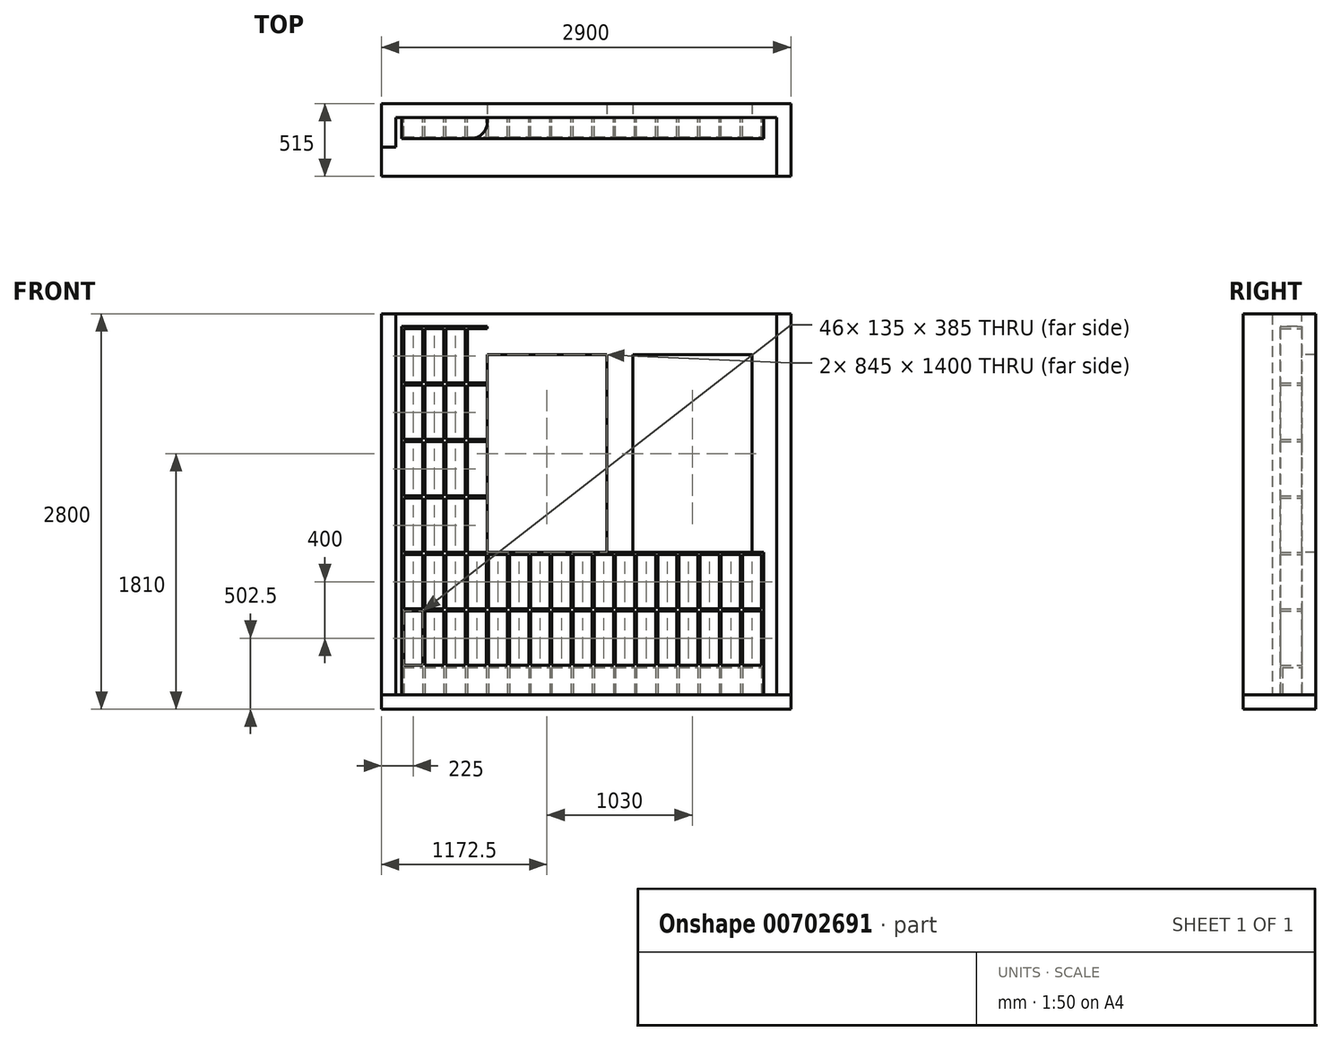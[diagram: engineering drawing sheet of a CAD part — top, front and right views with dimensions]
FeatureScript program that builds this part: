
annotation { "Feature Type Name" : "Feature", "Feature Type Description" : "" }
export const myFeature = defineFeature(function(context is Context, id is Id, definition is map)
    precondition{}
    {
        {
            var Q0;
            Q0=qCreatedBy(makeId("Front.planeOp"),FACE);
            var sketch = newSketch(context, id + "F0", { "sketchPlane" : qUnion([Q0])});
            skLineSegment(sketch, "E0.bottom", {"start": v(1350, -1350) * mm, "end": v(-1350, -1350) * mm});
            skLineSegment(sketch, "E0.top", {"start": v(1350, 1350) * mm, "end": v(-1350, 1350) * mm});
            skLineSegment(sketch, "E0.left", {"start": v(1350, -1350) * mm, "end": v(1350, 1350) * mm});
            skLineSegment(sketch, "E0.right", {"start": v(-1350, -1350) * mm, "end": v(-1350, 1350) * mm});
            skPoint(sketch, "E0.middle", {"position": v(0, 0) * mm});
            skLineSegment(sketch, "E1.bottom", {"start": v(1175, -340) * mm, "end": v(330, -340) * mm});
            skLineSegment(sketch, "E1.top", {"start": v(1175, 1060) * mm, "end": v(330, 1060) * mm});
            skLineSegment(sketch, "E1.left", {"start": v(1175, -340) * mm, "end": v(1175, 1060) * mm});
            skLineSegment(sketch, "E1.right", {"start": v(330, -340) * mm, "end": v(330, 1060) * mm});
            skPoint(sketch, "E1.middle", {"position": v(752.5, 360) * mm});
            skLineSegment(sketch, "E2.bottom", {"start": v(145, -340) * mm, "end": v(-700, -340) * mm});
            skLineSegment(sketch, "E2.top", {"start": v(145, 1060) * mm, "end": v(-700, 1060) * mm});
            skLineSegment(sketch, "E2.left", {"start": v(145, -340) * mm, "end": v(145, 1060) * mm});
            skLineSegment(sketch, "E2.right", {"start": v(-700, -340) * mm, "end": v(-700, 1060) * mm});
            skSolve(sketch);
        }
        {
            var Q0;
            Q0 = qSketchRegion(id + "F0", true);
            extrude(context, id + "F1", {"entities" : qUnion([Q0]), "oppositeDirection" : true, "depth" : 100 * mm, "offsetDistance" : 25 * mm});
        }
        {
            var Q0;
            Q0=qCreatedBy(makeId("Front.planeOp"),FACE);
            var sketch = newSketch(context, id + "F2", { "sketchPlane" : qUnion([Q0])});
            skLineSegment(sketch, "E3.top", {"start": v(-1307.5, -1350) * mm, "end": v(-1292.5, -1350) * mm});
            skLineSegment(sketch, "E4.top", {"start": v(-1157.5, -1350) * mm, "end": v(-1142.5, -1350) * mm});
            skLineSegment(sketch, "E5.MirrorCS", {"start": v(-992.5, -1350) * mm, "end": v(-1007.5, -1350) * mm});
            skLineSegment(sketch, "E6.MirrorCS", {"start": v(-842.5, -1350) * mm, "end": v(-857.5, -1350) * mm});
            skLineSegment(sketch, "E7.MirrorCS", {"start": v(-692.5, -355) * mm, "end": v(-692.5, -740) * mm});
            skLineSegment(sketch, "E8.MirrorCS", {"start": v(-557.5, -355) * mm, "end": v(-557.5, -740) * mm});
            skLineSegment(sketch, "E9.MirrorCS", {"start": v(-542.5, -355) * mm, "end": v(-542.5, -740) * mm});
            skLineSegment(sketch, "E10.MirrorCS", {"start": v(-707.5, -1350) * mm, "end": v(-692.5, -1350) * mm});
            skLineSegment(sketch, "E11.MirrorCS", {"start": v(-542.5, -1350) * mm, "end": v(-557.5, -1350) * mm});
            skLineSegment(sketch, "E12", {"start": v(-707.5, -340) * mm, "end": v(-692.5, -340) * mm});
            skLineSegment(sketch, "E13.trimOffspring", {"start": v(-707.5, -355) * mm, "end": v(-707.5, -740) * mm});
            skLineSegment(sketch, "E14", {"start": v(-557.5, -340) * mm, "end": v(-542.5, -340) * mm});
            skLineSegment(sketch, "E15.MirrorCS", {"start": v(-407.5, -355) * mm, "end": v(-407.5, -740) * mm});
            skLineSegment(sketch, "E16.MirrorCS", {"start": v(-392.5, -355) * mm, "end": v(-392.5, -740) * mm});
            skLineSegment(sketch, "E17.MirrorCS", {"start": v(-257.5, -355) * mm, "end": v(-257.5, -740) * mm});
            skLineSegment(sketch, "E18.MirrorCS", {"start": v(-242.5, -355) * mm, "end": v(-242.5, -740) * mm});
            skLineSegment(sketch, "E19.MirrorCS", {"start": v(-107.5, -355) * mm, "end": v(-107.5, -740) * mm});
            skLineSegment(sketch, "E20.MirrorCS", {"start": v(-92.5, -355) * mm, "end": v(-92.5, -740) * mm});
            skLineSegment(sketch, "E21", {"start": v(-257.5, -340) * mm, "end": v(-242.5, -340) * mm});
            skLineSegment(sketch, "E22", {"start": v(-407.5, -1350) * mm, "end": v(-392.5, -1350) * mm});
            skLineSegment(sketch, "E23", {"start": v(-257.5, -1350) * mm, "end": v(-242.5, -1350) * mm});
            skLineSegment(sketch, "E24", {"start": v(-107.5, -1350) * mm, "end": v(-92.5, -1350) * mm});
            skLineSegment(sketch, "E25.MirrorCS", {"start": v(42.5, -355) * mm, "end": v(42.5, -740) * mm});
            skLineSegment(sketch, "E26.MirrorCS", {"start": v(57.5, -355) * mm, "end": v(57.5, -740) * mm});
            skLineSegment(sketch, "E27.MirrorCS", {"start": v(192.5, -355) * mm, "end": v(192.5, -740) * mm});
            skLineSegment(sketch, "E28.MirrorCS", {"start": v(207.5, -355) * mm, "end": v(207.5, -740) * mm});
            skLineSegment(sketch, "E29.MirrorCS", {"start": v(342.5, -355) * mm, "end": v(342.5, -740) * mm});
            skLineSegment(sketch, "E30.MirrorCS", {"start": v(357.5, -355) * mm, "end": v(357.5, -740) * mm});
            skLineSegment(sketch, "E31.MirrorCS", {"start": v(492.5, -355) * mm, "end": v(492.5, -740) * mm});
            skLineSegment(sketch, "E32.MirrorCS", {"start": v(507.5, -355) * mm, "end": v(507.5, -740) * mm});
            skLineSegment(sketch, "E33", {"start": v(42.5, -1350) * mm, "end": v(57.5, -1350) * mm});
            skLineSegment(sketch, "E34", {"start": v(192.5, -1350) * mm, "end": v(207.5, -1350) * mm});
            skLineSegment(sketch, "E35", {"start": v(342.5, -1350) * mm, "end": v(357.5, -1350) * mm});
            skLineSegment(sketch, "E36", {"start": v(492.5, -1350) * mm, "end": v(507.5, -1350) * mm});
            skLineSegment(sketch, "E37", {"start": v(-107.5, -340) * mm, "end": v(-92.5, -340) * mm});
            skLineSegment(sketch, "E38", {"start": v(42.5, -340) * mm, "end": v(57.5, -340) * mm});
            skLineSegment(sketch, "E39", {"start": v(192.5, -340) * mm, "end": v(207.5, -340) * mm});
            skLineSegment(sketch, "E40", {"start": v(342.5, -340) * mm, "end": v(357.5, -340) * mm});
            skLineSegment(sketch, "E41", {"start": v(492.5, -340) * mm, "end": v(507.5, -340) * mm});
            skLineSegment(sketch, "E42.MirrorCS", {"start": v(642.5, -355) * mm, "end": v(642.5, -740) * mm});
            skLineSegment(sketch, "E43.MirrorCS", {"start": v(657.5, -355) * mm, "end": v(657.5, -740) * mm});
            skLineSegment(sketch, "E44.MirrorCS", {"start": v(792.5, -355) * mm, "end": v(792.5, -740) * mm});
            skLineSegment(sketch, "E45.MirrorCS", {"start": v(807.5, -355) * mm, "end": v(807.5, -740) * mm});
            skLineSegment(sketch, "E46.MirrorCS", {"start": v(942.5, -355) * mm, "end": v(942.5, -740) * mm});
            skLineSegment(sketch, "E47.MirrorCS", {"start": v(957.5, -355) * mm, "end": v(957.5, -740) * mm});
            skLineSegment(sketch, "E48.MirrorCS", {"start": v(1092.5, -355) * mm, "end": v(1092.5, -740) * mm});
            skLineSegment(sketch, "E49.MirrorCS", {"start": v(1107.5, -355) * mm, "end": v(1107.5, -740) * mm});
            skLineSegment(sketch, "E50.MirrorCS", {"start": v(1242.5, -355) * mm, "end": v(1242.5, -740) * mm});
            skLineSegment(sketch, "E51", {"start": v(642.5, -340) * mm, "end": v(657.5, -340) * mm});
            skLineSegment(sketch, "E52", {"start": v(792.5, -340) * mm, "end": v(807.5, -340) * mm});
            skLineSegment(sketch, "E53", {"start": v(942.5, -340) * mm, "end": v(957.5, -340) * mm});
            skLineSegment(sketch, "E54", {"start": v(1092.5, -340) * mm, "end": v(1107.5, -340) * mm});
            skLineSegment(sketch, "E55", {"start": v(1242.5, -340) * mm, "end": v(1257.5, -340) * mm});
            skLineSegment(sketch, "E56", {"start": v(642.5, -1350) * mm, "end": v(657.5, -1350) * mm});
            skLineSegment(sketch, "E57", {"start": v(792.5, -1350) * mm, "end": v(807.5, -1350) * mm});
            skLineSegment(sketch, "E58", {"start": v(942.5, -1350) * mm, "end": v(957.5, -1350) * mm});
            skLineSegment(sketch, "E59", {"start": v(1092.5, -1350) * mm, "end": v(1107.5, -1350) * mm});
            skLineSegment(sketch, "E60", {"start": v(-407.5, -340) * mm, "end": v(-392.5, -340) * mm});
            skLineSegment(sketch, "E61.right", {"start": v(-700, 60) * mm, "end": v(-700, 45) * mm});
            skLineSegment(sketch, "E62.right", {"start": v(-700, 460) * mm, "end": v(-700, 445) * mm});
            skLineSegment(sketch, "E63.right", {"start": v(-700, 860) * mm, "end": v(-700, 845) * mm});
            skLineSegment(sketch, "E64.right", {"start": v(-699.99, 1260) * mm, "end": v(-700, 1245) * mm});
            skLineSegment(sketch, "E65", {"start": v(942.5, -740) * mm, "end": v(957.5, -740) * mm});
            skLineSegment(sketch, "E66.trimOffspring", {"start": v(-1292.5, -755) * mm, "end": v(-1292.5, -1140) * mm});
            skLineSegment(sketch, "E67.trimOffspring", {"start": v(-1292.5, -755) * mm, "end": v(-1157.5, -755) * mm});
            skLineSegment(sketch, "E68.trimOffspring", {"start": v(-1292.5, -740) * mm, "end": v(-1157.5, -740) * mm});
            skLineSegment(sketch, "E69.trimOffspring", {"start": v(-1157.5, -755) * mm, "end": v(-1157.5, -1140) * mm});
            skLineSegment(sketch, "E70.trimOffspring", {"start": v(-1142.5, -740) * mm, "end": v(-1007.5, -740) * mm});
            skLineSegment(sketch, "E71.trimOffspring", {"start": v(-1142.5, -755) * mm, "end": v(-1142.5, -1140) * mm});
            skLineSegment(sketch, "E72.trimOffspring", {"start": v(-1292.5, 1245) * mm, "end": v(-1292.5, 860) * mm});
            skLineSegment(sketch, "E73.trimOffspring", {"start": v(-1292.5, 1245) * mm, "end": v(-1157.5, 1245) * mm});
            skLineSegment(sketch, "E74.trimOffspring", {"start": v(-1157.5, 1245) * mm, "end": v(-1157.5, 860) * mm});
            skLineSegment(sketch, "E75.trimOffspring", {"start": v(-1142.5, 1245) * mm, "end": v(-1007.5, 1245) * mm});
            skLineSegment(sketch, "E76.trimOffspring", {"start": v(-1007.5, 1245) * mm, "end": v(-1007.5, 860) * mm});
            skLineSegment(sketch, "E77.trimOffspring", {"start": v(-992.5, 1245) * mm, "end": v(-992.5, 860) * mm});
            skLineSegment(sketch, "E78.trimOffspring", {"start": v(-992.5, 1245) * mm, "end": v(-857.5, 1245) * mm});
            skLineSegment(sketch, "E79.trimOffspring", {"start": v(-857.5, 1245) * mm, "end": v(-857.5, 860) * mm});
            skLineSegment(sketch, "E80.trimOffspring", {"start": v(-842.5, 1245) * mm, "end": v(-842.5, 860) * mm});
            skLineSegment(sketch, "E81.trimOffspring", {"start": v(-842.5, 1245) * mm, "end": v(-700, 1245) * mm});
            skLineSegment(sketch, "E82.trimOffspring", {"start": v(-1157.5, 845) * mm, "end": v(-1157.5, 460) * mm});
            skLineSegment(sketch, "E83.trimOffspring", {"start": v(-1142.5, 860) * mm, "end": v(-1007.5, 860) * mm});
            skLineSegment(sketch, "E84.trimOffspring", {"start": v(-1142.5, 845) * mm, "end": v(-1142.5, 460) * mm});
            skLineSegment(sketch, "E85.trimOffspring", {"start": v(-1142.5, 845) * mm, "end": v(-1007.5, 845) * mm});
            skLineSegment(sketch, "E86.trimOffspring", {"start": v(-1292.5, 445) * mm, "end": v(-1292.5, 60) * mm});
            skLineSegment(sketch, "E87.trimOffspring", {"start": v(-1292.5, 860) * mm, "end": v(-1157.5, 860) * mm});
            skLineSegment(sketch, "E88.trimOffspring", {"start": v(-1292.5, 845) * mm, "end": v(-1157.5, 845) * mm});
            skLineSegment(sketch, "E89", {"start": v(-1142.5, 1245) * mm, "end": v(-1142.5, 860) * mm});
            skLineSegment(sketch, "E90.trimOffspring", {"start": v(-992.5, 845) * mm, "end": v(-992.5, 460) * mm});
            skLineSegment(sketch, "E91.trimOffspring", {"start": v(-992.5, 860) * mm, "end": v(-857.5, 860) * mm});
            skLineSegment(sketch, "E92.trimOffspring", {"start": v(-1007.5, 845) * mm, "end": v(-1007.5, 460) * mm});
            skLineSegment(sketch, "E93.trimOffspring", {"start": v(-992.5, 845) * mm, "end": v(-857.5, 845) * mm});
            skLineSegment(sketch, "E94.trimOffspring", {"start": v(-842.5, 845) * mm, "end": v(-842.5, 460) * mm});
            skLineSegment(sketch, "E95.trimOffspring", {"start": v(-857.5, 845) * mm, "end": v(-857.5, 460) * mm});
            skLineSegment(sketch, "E96.trimOffspring", {"start": v(-842.5, 860) * mm, "end": v(-700, 860) * mm});
            skLineSegment(sketch, "E97.trimOffspring", {"start": v(-842.5, 845) * mm, "end": v(-700, 845) * mm});
            skLineSegment(sketch, "E98", {"start": v(-1292.5, 845) * mm, "end": v(-1292.5, 460) * mm});
            skLineSegment(sketch, "E99.trimOffspring", {"start": v(-1292.5, 460) * mm, "end": v(-1157.5, 460) * mm});
            skLineSegment(sketch, "E100.trimOffspring", {"start": v(-1292.5, 445) * mm, "end": v(-1157.5, 445) * mm});
            skLineSegment(sketch, "E101.trimOffspring", {"start": v(-1142.5, 445) * mm, "end": v(-1142.5, 60) * mm});
            skLineSegment(sketch, "E102.trimOffspring", {"start": v(-1157.5, 445) * mm, "end": v(-1157.5, 60) * mm});
            skLineSegment(sketch, "E103.trimOffspring", {"start": v(-1142.5, 460) * mm, "end": v(-1007.5, 460) * mm});
            skLineSegment(sketch, "E104.trimOffspring", {"start": v(-1142.5, 445) * mm, "end": v(-1007.5, 445) * mm});
            skLineSegment(sketch, "E105.trimOffspring", {"start": v(-1007.5, 445) * mm, "end": v(-1007.5, 60) * mm});
            skLineSegment(sketch, "E106.trimOffspring", {"start": v(-992.5, 460) * mm, "end": v(-857.5, 460) * mm});
            skLineSegment(sketch, "E107.trimOffspring", {"start": v(-992.5, 445) * mm, "end": v(-992.5, 60) * mm});
            skLineSegment(sketch, "E108.trimOffspring", {"start": v(-992.5, 445) * mm, "end": v(-857.5, 445) * mm});
            skLineSegment(sketch, "E109.trimOffspring", {"start": v(-842.5, 445) * mm, "end": v(-842.5, 60) * mm});
            skLineSegment(sketch, "E110.trimOffspring", {"start": v(-842.5, 460) * mm, "end": v(-700, 460) * mm});
            skLineSegment(sketch, "E111.trimOffspring", {"start": v(-842.5, 445) * mm, "end": v(-700, 445) * mm});
            skLineSegment(sketch, "E112.trimOffspring", {"start": v(-857.5, 445) * mm, "end": v(-857.5, 60) * mm});
            skLineSegment(sketch, "E113.trimOffspring", {"start": v(-842.5, 45) * mm, "end": v(-842.5, -340) * mm});
            skLineSegment(sketch, "E114.trimOffspring", {"start": v(-857.5, 45) * mm, "end": v(-857.5, -340) * mm});
            skLineSegment(sketch, "E115.trimOffspring", {"start": v(-842.5, 60) * mm, "end": v(-700, 60) * mm});
            skLineSegment(sketch, "E116.trimOffspring", {"start": v(-842.5, 45) * mm, "end": v(-700, 45) * mm});
            skLineSegment(sketch, "E117.trimOffspring", {"start": v(-992.5, 45) * mm, "end": v(-992.5, -340) * mm});
            skLineSegment(sketch, "E118.trimOffspring", {"start": v(-992.5, 60) * mm, "end": v(-857.5, 60) * mm});
            skLineSegment(sketch, "E119.trimOffspring", {"start": v(-1007.5, 45) * mm, "end": v(-1007.5, -340) * mm});
            skLineSegment(sketch, "E120.trimOffspring", {"start": v(-992.5, 45) * mm, "end": v(-857.5, 45) * mm});
            skLineSegment(sketch, "E121.trimOffspring", {"start": v(-1142.5, 60) * mm, "end": v(-1007.5, 60) * mm});
            skLineSegment(sketch, "E122.trimOffspring", {"start": v(-1157.5, 45) * mm, "end": v(-1157.5, -340) * mm});
            skLineSegment(sketch, "E123.trimOffspring", {"start": v(-1142.5, 45) * mm, "end": v(-1007.5, 45) * mm});
            skLineSegment(sketch, "E124.trimOffspring", {"start": v(-1142.5, 45) * mm, "end": v(-1142.5, -340) * mm});
            skLineSegment(sketch, "E125.trimOffspring", {"start": v(-1292.5, 60) * mm, "end": v(-1157.5, 60) * mm});
            skLineSegment(sketch, "E126.trimOffspring", {"start": v(-1292.5, 45) * mm, "end": v(-1157.5, 45) * mm});
            skLineSegment(sketch, "E127.trimOffspring", {"start": v(-1292.5, 45) * mm, "end": v(-1292.5, -340) * mm});
            skLineSegment(sketch, "E128.trimOffspring", {"start": v(-1292.5, -355) * mm, "end": v(-1292.5, -740) * mm});
            skLineSegment(sketch, "E129.trimOffspring", {"start": v(-1157.5, -355) * mm, "end": v(-1157.5, -740) * mm});
            skLineSegment(sketch, "E130.trimOffspring", {"start": v(-1142.5, -355) * mm, "end": v(-1142.5, -740) * mm});
            skLineSegment(sketch, "E131.trimOffspring", {"start": v(-992.5, -355) * mm, "end": v(-992.5, -740) * mm});
            skLineSegment(sketch, "E132.trimOffspring", {"start": v(-1007.5, -355) * mm, "end": v(-1007.5, -740) * mm});
            skLineSegment(sketch, "E133.trimOffspring", {"start": v(-857.5, -355) * mm, "end": v(-857.5, -740) * mm});
            skLineSegment(sketch, "E134.trimOffspring", {"start": v(-842.5, -355) * mm, "end": v(-842.5, -740) * mm});
            skLineSegment(sketch, "E135.trimOffspring", {"start": v(-692.5, -340) * mm, "end": v(-257.5, -340) * mm});
            skLineSegment(sketch, "E136.trimOffspring", {"start": v(-1007.5, -755) * mm, "end": v(-1007.5, -1140) * mm});
            skLineSegment(sketch, "E137.trimOffspring", {"start": v(-992.5, -755) * mm, "end": v(-992.5, -1140) * mm});
            skLineSegment(sketch, "E138.trimOffspring", {"start": v(-857.5, -755) * mm, "end": v(-857.5, -1140) * mm});
            skLineSegment(sketch, "E139.trimOffspring", {"start": v(-842.5, -755) * mm, "end": v(-842.5, -1140) * mm});
            skLineSegment(sketch, "E140.trimOffspring", {"start": v(-542.5, -755) * mm, "end": v(-542.5, -1140) * mm});
            skLineSegment(sketch, "E141.trimOffspring", {"start": v(-557.5, -755) * mm, "end": v(-557.5, -1140) * mm});
            skLineSegment(sketch, "E142.trimOffspring", {"start": v(-407.5, -755) * mm, "end": v(-407.5, -1140) * mm});
            skLineSegment(sketch, "E143.trimOffspring", {"start": v(-392.5, -755) * mm, "end": v(-392.5, -1140) * mm});
            skLineSegment(sketch, "E144.trimOffspring", {"start": v(-242.5, -755) * mm, "end": v(-242.5, -1140) * mm});
            skLineSegment(sketch, "E145.trimOffspring", {"start": v(-257.5, -755) * mm, "end": v(-257.5, -1140) * mm});
            skLineSegment(sketch, "E146.trimOffspring", {"start": v(-92.5, -755) * mm, "end": v(-92.5, -1140) * mm});
            skLineSegment(sketch, "E147.trimOffspring", {"start": v(-107.5, -755) * mm, "end": v(-107.5, -1140) * mm});
            skLineSegment(sketch, "E148.trimOffspring", {"start": v(57.5, -755) * mm, "end": v(57.5, -1140) * mm});
            skLineSegment(sketch, "E149.trimOffspring", {"start": v(42.5, -755) * mm, "end": v(42.5, -1140) * mm});
            skLineSegment(sketch, "E150.trimOffspring", {"start": v(207.5, -755) * mm, "end": v(207.5, -1140) * mm});
            skLineSegment(sketch, "E151.trimOffspring", {"start": v(192.5, -755) * mm, "end": v(192.5, -1140) * mm});
            skLineSegment(sketch, "E152.trimOffspring", {"start": v(342.5, -755) * mm, "end": v(342.5, -1140) * mm});
            skLineSegment(sketch, "E153.trimOffspring", {"start": v(357.5, -755) * mm, "end": v(357.5, -1140) * mm});
            skLineSegment(sketch, "E154.trimOffspring", {"start": v(492.5, -755) * mm, "end": v(492.5, -1140) * mm});
            skLineSegment(sketch, "E155.trimOffspring", {"start": v(507.5, -755) * mm, "end": v(507.5, -1140) * mm});
            skLineSegment(sketch, "E156.trimOffspring", {"start": v(657.5, -755) * mm, "end": v(657.5, -1140) * mm});
            skLineSegment(sketch, "E157.trimOffspring", {"start": v(642.5, -755) * mm, "end": v(642.5, -1140) * mm});
            skLineSegment(sketch, "E158.trimOffspring", {"start": v(792.5, -755) * mm, "end": v(792.5, -1140) * mm});
            skLineSegment(sketch, "E159.trimOffspring", {"start": v(807.5, -755) * mm, "end": v(807.5, -1140) * mm});
            skLineSegment(sketch, "E160.trimOffspring", {"start": v(957.5, -755) * mm, "end": v(957.5, -1140) * mm});
            skLineSegment(sketch, "E161.trimOffspring", {"start": v(1092.5, -755) * mm, "end": v(1092.5, -1140) * mm});
            skLineSegment(sketch, "E162.trimOffspring", {"start": v(942.5, -755) * mm, "end": v(942.5, -1140) * mm});
            skLineSegment(sketch, "E163.trimOffspring", {"start": v(1107.5, -755) * mm, "end": v(1107.5, -1140) * mm});
            skLineSegment(sketch, "E164.trimOffspring", {"start": v(1242.5, -755) * mm, "end": v(1242.5, -1140) * mm});
            skLineSegment(sketch, "E165.trimOffspring", {"start": v(-692.5, -755) * mm, "end": v(-692.5, -1140) * mm});
            skLineSegment(sketch, "E166.trimOffspring", {"start": v(-707.5, -755) * mm, "end": v(-707.5, -1140) * mm});
            skLineSegment(sketch, "E167.trimOffspring", {"start": v(-692.5, -355) * mm, "end": v(-557.5, -355) * mm});
            skLineSegment(sketch, "E168.trimOffspring", {"start": v(-542.5, -355) * mm, "end": v(-407.5, -355) * mm});
            skLineSegment(sketch, "E169.trimOffspring", {"start": v(-992.5, -355) * mm, "end": v(-857.5, -355) * mm});
            skLineSegment(sketch, "E170.trimOffspring", {"start": v(-1142.5, -355) * mm, "end": v(-1007.5, -355) * mm});
            skLineSegment(sketch, "E171.trimOffspring", {"start": v(-842.5, -355) * mm, "end": v(-707.5, -355) * mm});
            skLineSegment(sketch, "E172.trimOffspring", {"start": v(-992.5, -740) * mm, "end": v(-857.5, -740) * mm});
            skLineSegment(sketch, "E173.trimOffspring", {"start": v(-842.5, -740) * mm, "end": v(-707.5, -740) * mm});
            skLineSegment(sketch, "E174.trimOffspring", {"start": v(-992.5, -755) * mm, "end": v(-857.5, -755) * mm});
            skLineSegment(sketch, "E175.trimOffspring", {"start": v(-692.5, -740) * mm, "end": v(-557.5, -740) * mm});
            skLineSegment(sketch, "E176.trimOffspring", {"start": v(-692.5, -755) * mm, "end": v(-557.5, -755) * mm});
            skLineSegment(sketch, "E177.trimOffspring", {"start": v(-542.5, -755) * mm, "end": v(-407.5, -755) * mm});
            skLineSegment(sketch, "E178.trimOffspring", {"start": v(-542.5, -740) * mm, "end": v(-407.5, -740) * mm});
            skLineSegment(sketch, "E179.trimOffspring", {"start": v(-392.5, -755) * mm, "end": v(-257.5, -755) * mm});
            skLineSegment(sketch, "E180.trimOffspring", {"start": v(-707.5, -1155) * mm, "end": v(-707.5, -1350) * mm});
            skLineSegment(sketch, "E181.trimOffspring", {"start": v(-692.5, -1155) * mm, "end": v(-692.5, -1350) * mm});
            skLineSegment(sketch, "E182", {"start": v(-1142.5, -755) * mm, "end": v(-1007.5, -755) * mm});
            skLineSegment(sketch, "E183.trimOffspring", {"start": v(-1292.5, -1140) * mm, "end": v(-1157.5, -1140) * mm});
            skLineSegment(sketch, "E184.trimOffspring", {"start": v(-1292.5, -1155) * mm, "end": v(-1157.5, -1155) * mm});
            skLineSegment(sketch, "E185.trimOffspring", {"start": v(-1292.5, -1155) * mm, "end": v(-1292.5, -1350) * mm});
            skLineSegment(sketch, "E186.trimOffspring", {"start": v(-1142.5, -1155) * mm, "end": v(-1142.5, -1350) * mm});
            skLineSegment(sketch, "E187.trimOffspring", {"start": v(-1157.5, -1155) * mm, "end": v(-1157.5, -1350) * mm});
            skLineSegment(sketch, "E188.trimOffspring", {"start": v(-1142.5, -1140) * mm, "end": v(-1007.5, -1140) * mm});
            skLineSegment(sketch, "E189.trimOffspring", {"start": v(-1142.5, -1155) * mm, "end": v(-1007.5, -1155) * mm});
            skLineSegment(sketch, "E190.trimOffspring", {"start": v(-992.5, -1140) * mm, "end": v(-857.5, -1140) * mm});
            skLineSegment(sketch, "E191.trimOffspring", {"start": v(-1007.5, -1155) * mm, "end": v(-1007.5, -1350) * mm});
            skLineSegment(sketch, "E192.trimOffspring", {"start": v(-992.5, -1155) * mm, "end": v(-857.5, -1155) * mm});
            skLineSegment(sketch, "E193.trimOffspring", {"start": v(-992.5, -1155) * mm, "end": v(-992.5, -1350) * mm});
            skLineSegment(sketch, "E194.trimOffspring", {"start": v(-842.5, -1140) * mm, "end": v(-707.5, -1140) * mm});
            skLineSegment(sketch, "E195.trimOffspring", {"start": v(-857.5, -1155) * mm, "end": v(-857.5, -1350) * mm});
            skLineSegment(sketch, "E196.trimOffspring", {"start": v(-842.5, -1155) * mm, "end": v(-707.5, -1155) * mm});
            skLineSegment(sketch, "E197.trimOffspring", {"start": v(-842.5, -1155) * mm, "end": v(-842.5, -1350) * mm});
            skLineSegment(sketch, "E198.trimOffspring", {"start": v(-392.5, -355) * mm, "end": v(-257.5, -355) * mm});
            skLineSegment(sketch, "E199.trimOffspring", {"start": v(-242.5, -355) * mm, "end": v(-107.5, -355) * mm});
            skLineSegment(sketch, "E200.trimOffspring", {"start": v(-92.5, -355) * mm, "end": v(192.5, -355) * mm});
            skLineSegment(sketch, "E201.trimOffspring", {"start": v(-242.5, -340) * mm, "end": v(-107.5, -340) * mm});
            skLineSegment(sketch, "E202.trimOffspring", {"start": v(-92.5, -340) * mm, "end": v(1257.5, -340) * mm});
            skLineSegment(sketch, "E203.trimOffspring", {"start": v(207.5, -355) * mm, "end": v(342.5, -355) * mm});
            skLineSegment(sketch, "E204.trimOffspring", {"start": v(357.5, -355) * mm, "end": v(492.5, -355) * mm});
            skLineSegment(sketch, "E205.trimOffspring", {"start": v(507.5, -355) * mm, "end": v(642.5, -355) * mm});
            skLineSegment(sketch, "E206.trimOffspring", {"start": v(657.5, -355) * mm, "end": v(792.5, -355) * mm});
            skLineSegment(sketch, "E207.trimOffspring", {"start": v(807.5, -355) * mm, "end": v(942.5, -355) * mm});
            skLineSegment(sketch, "E208.trimOffspring", {"start": v(957.5, -355) * mm, "end": v(1092.5, -355) * mm});
            skLineSegment(sketch, "E209.trimOffspring", {"start": v(1107.5, -355) * mm, "end": v(1242.5, -355) * mm});
            skLineSegment(sketch, "E210.trimOffspring", {"start": v(1107.5, -740) * mm, "end": v(1242.5, -740) * mm});
            skLineSegment(sketch, "E211.trimOffspring", {"start": v(1107.5, -755) * mm, "end": v(1242.5, -755) * mm});
            skLineSegment(sketch, "E212.trimOffspring", {"start": v(957.5, -755) * mm, "end": v(1092.5, -755) * mm});
            skLineSegment(sketch, "E213.trimOffspring", {"start": v(957.5, -740) * mm, "end": v(1092.5, -740) * mm});
            skLineSegment(sketch, "E214.trimOffspring", {"start": v(807.5, -755) * mm, "end": v(942.5, -755) * mm});
            skLineSegment(sketch, "E215.trimOffspring", {"start": v(807.5, -740) * mm, "end": v(942.5, -740) * mm});
            skLineSegment(sketch, "E216.trimOffspring", {"start": v(657.5, -755) * mm, "end": v(792.5, -755) * mm});
            skLineSegment(sketch, "E217.trimOffspring", {"start": v(657.5, -740) * mm, "end": v(792.5, -740) * mm});
            skLineSegment(sketch, "E218.trimOffspring", {"start": v(507.5, -740) * mm, "end": v(642.5, -740) * mm});
            skLineSegment(sketch, "E219.trimOffspring", {"start": v(507.5, -755) * mm, "end": v(642.5, -755) * mm});
            skLineSegment(sketch, "E220.trimOffspring", {"start": v(357.5, -740) * mm, "end": v(492.5, -740) * mm});
            skLineSegment(sketch, "E221.trimOffspring", {"start": v(357.5, -755) * mm, "end": v(492.5, -755) * mm});
            skLineSegment(sketch, "E222.trimOffspring", {"start": v(207.5, -740) * mm, "end": v(342.5, -740) * mm});
            skLineSegment(sketch, "E223.trimOffspring", {"start": v(207.5, -755) * mm, "end": v(342.5, -755) * mm});
            skLineSegment(sketch, "E224.trimOffspring", {"start": v(57.5, -740) * mm, "end": v(192.5, -740) * mm});
            skLineSegment(sketch, "E225.trimOffspring", {"start": v(57.5, -755) * mm, "end": v(192.5, -755) * mm});
            skLineSegment(sketch, "E226.trimOffspring", {"start": v(-92.5, -740) * mm, "end": v(42.5, -740) * mm});
            skLineSegment(sketch, "E227.trimOffspring", {"start": v(-92.5, -755) * mm, "end": v(42.5, -755) * mm});
            skLineSegment(sketch, "E228.trimOffspring", {"start": v(-242.5, -740) * mm, "end": v(-107.5, -740) * mm});
            skLineSegment(sketch, "E229.trimOffspring", {"start": v(-242.5, -755) * mm, "end": v(-107.5, -755) * mm});
            skLineSegment(sketch, "E230.trimOffspring", {"start": v(-392.5, -740) * mm, "end": v(-257.5, -740) * mm});
            skLineSegment(sketch, "E231.trimOffspring", {"start": v(-692.5, -1140) * mm, "end": v(-557.5, -1140) * mm});
            skLineSegment(sketch, "E232.trimOffspring", {"start": v(-692.5, -1155) * mm, "end": v(-557.5, -1155) * mm});
            skLineSegment(sketch, "E233.trimOffspring", {"start": v(-542.5, -1140) * mm, "end": v(-407.5, -1140) * mm});
            skLineSegment(sketch, "E234.trimOffspring", {"start": v(-542.5, -1155) * mm, "end": v(-407.5, -1155) * mm});
            skLineSegment(sketch, "E235.trimOffspring", {"start": v(-542.5, -1155) * mm, "end": v(-542.5, -1350) * mm});
            skLineSegment(sketch, "E236.trimOffspring", {"start": v(-557.5, -1155) * mm, "end": v(-557.5, -1350) * mm});
            skLineSegment(sketch, "E237.trimOffspring", {"start": v(-407.5, -1155) * mm, "end": v(-407.5, -1350) * mm});
            skLineSegment(sketch, "E238.trimOffspring", {"start": v(-392.5, -1140) * mm, "end": v(-257.5, -1140) * mm});
            skLineSegment(sketch, "E239.trimOffspring", {"start": v(-392.5, -1155) * mm, "end": v(-392.5, -1350) * mm});
            skLineSegment(sketch, "E240.trimOffspring", {"start": v(-392.5, -1155) * mm, "end": v(-257.5, -1155) * mm});
            skLineSegment(sketch, "E241.trimOffspring", {"start": v(-257.5, -1155) * mm, "end": v(-257.5, -1350) * mm});
            skLineSegment(sketch, "E242.trimOffspring", {"start": v(-242.5, -1140) * mm, "end": v(-107.5, -1140) * mm});
            skLineSegment(sketch, "E243.trimOffspring", {"start": v(-242.5, -1155) * mm, "end": v(-242.5, -1350) * mm});
            skLineSegment(sketch, "E244.trimOffspring", {"start": v(-242.5, -1155) * mm, "end": v(-107.5, -1155) * mm});
            skLineSegment(sketch, "E245.trimOffspring", {"start": v(-107.5, -1155) * mm, "end": v(-107.5, -1350) * mm});
            skLineSegment(sketch, "E246.trimOffspring", {"start": v(-92.5, -1155) * mm, "end": v(42.5, -1155) * mm});
            skLineSegment(sketch, "E247.trimOffspring", {"start": v(-92.5, -1155) * mm, "end": v(-92.5, -1350) * mm});
            skLineSegment(sketch, "E248.trimOffspring", {"start": v(-92.5, -1140) * mm, "end": v(42.5, -1140) * mm});
            skLineSegment(sketch, "E249.trimOffspring", {"start": v(42.5, -1155) * mm, "end": v(42.5, -1350) * mm});
            skLineSegment(sketch, "E250.trimOffspring", {"start": v(57.5, -1140) * mm, "end": v(192.5, -1140) * mm});
            skLineSegment(sketch, "E251.trimOffspring", {"start": v(57.5, -1155) * mm, "end": v(192.5, -1155) * mm});
            skLineSegment(sketch, "E252.trimOffspring", {"start": v(57.5, -1155) * mm, "end": v(57.5, -1350) * mm});
            skLineSegment(sketch, "E253.trimOffspring", {"start": v(192.5, -1155) * mm, "end": v(192.5, -1350) * mm});
            skLineSegment(sketch, "E254.trimOffspring", {"start": v(207.5, -1155) * mm, "end": v(207.5, -1350) * mm});
            skLineSegment(sketch, "E255.trimOffspring", {"start": v(207.5, -1155) * mm, "end": v(342.5, -1155) * mm});
            skLineSegment(sketch, "E256.trimOffspring", {"start": v(207.5, -1140) * mm, "end": v(342.5, -1140) * mm});
            skLineSegment(sketch, "E257.trimOffspring", {"start": v(357.5, -1140) * mm, "end": v(492.5, -1140) * mm});
            skLineSegment(sketch, "E258.trimOffspring", {"start": v(342.5, -1155) * mm, "end": v(342.5, -1350) * mm});
            skLineSegment(sketch, "E259.trimOffspring", {"start": v(357.5, -1155) * mm, "end": v(492.5, -1155) * mm});
            skLineSegment(sketch, "E260.trimOffspring", {"start": v(357.5, -1155) * mm, "end": v(357.5, -1350) * mm});
            skLineSegment(sketch, "E261.trimOffspring", {"start": v(507.5, -1140) * mm, "end": v(642.5, -1140) * mm});
            skLineSegment(sketch, "E262.trimOffspring", {"start": v(492.5, -1155) * mm, "end": v(492.5, -1350) * mm});
            skLineSegment(sketch, "E263.trimOffspring", {"start": v(507.5, -1155) * mm, "end": v(507.5, -1350) * mm});
            skLineSegment(sketch, "E264.trimOffspring", {"start": v(507.5, -1155) * mm, "end": v(642.5, -1155) * mm});
            skLineSegment(sketch, "E265.trimOffspring", {"start": v(642.5, -1155) * mm, "end": v(642.5, -1350) * mm});
            skLineSegment(sketch, "E266.trimOffspring", {"start": v(657.5, -1155) * mm, "end": v(657.5, -1350) * mm});
            skLineSegment(sketch, "E267.trimOffspring", {"start": v(657.5, -1155) * mm, "end": v(792.5, -1155) * mm});
            skLineSegment(sketch, "E268.trimOffspring", {"start": v(657.5, -1140) * mm, "end": v(792.5, -1140) * mm});
            skLineSegment(sketch, "E269.trimOffspring", {"start": v(807.5, -1140) * mm, "end": v(942.5, -1140) * mm});
            skLineSegment(sketch, "E270.trimOffspring", {"start": v(792.5, -1155) * mm, "end": v(792.5, -1350) * mm});
            skLineSegment(sketch, "E271.trimOffspring", {"start": v(807.5, -1155) * mm, "end": v(942.5, -1155) * mm});
            skLineSegment(sketch, "E272.trimOffspring", {"start": v(807.5, -1155) * mm, "end": v(807.5, -1350) * mm});
            skLineSegment(sketch, "E273.trimOffspring", {"start": v(957.5, -1140) * mm, "end": v(1092.5, -1140) * mm});
            skLineSegment(sketch, "E274.trimOffspring", {"start": v(942.5, -1155) * mm, "end": v(942.5, -1350) * mm});
            skLineSegment(sketch, "E275.trimOffspring", {"start": v(957.5, -1155) * mm, "end": v(1092.5, -1155) * mm});
            skLineSegment(sketch, "E276.trimOffspring", {"start": v(957.5, -1155) * mm, "end": v(957.5, -1350) * mm});
            skLineSegment(sketch, "E277.trimOffspring", {"start": v(1107.5, -1140) * mm, "end": v(1242.5, -1140) * mm});
            skLineSegment(sketch, "E278.trimOffspring", {"start": v(1092.5, -1155) * mm, "end": v(1092.5, -1350) * mm});
            skLineSegment(sketch, "E279.trimOffspring", {"start": v(1107.5, -1155) * mm, "end": v(1242.5, -1155) * mm});
            skLineSegment(sketch, "E280.trimOffspring", {"start": v(1107.5, -1155) * mm, "end": v(1107.5, -1350) * mm});
            skLineSegment(sketch, "E281.trimOffspring", {"start": v(1242.5, -1155) * mm, "end": v(1242.5, -1350) * mm});
            skLineSegment(sketch, "E282.trimOffspring", {"start": v(1257.5, -340) * mm, "end": v(1257.5, -1350) * mm});
            skLineSegment(sketch, "E283.trimOffspring", {"start": v(-1142.5, -340) * mm, "end": v(-1007.5, -340) * mm});
            skLineSegment(sketch, "E284.trimOffspring", {"start": v(-992.5, -340) * mm, "end": v(-857.5, -340) * mm});
            skLineSegment(sketch, "E285.trimOffspring", {"start": v(-1292.5, -340) * mm, "end": v(-1157.5, -340) * mm});
            skLineSegment(sketch, "E286.trimOffspring", {"start": v(-842.5, -340) * mm, "end": v(-707.5, -340) * mm});
            skLineSegment(sketch, "E287.trimOffspring", {"start": v(-1292.5, -355) * mm, "end": v(-1157.5, -355) * mm});
            skLineSegment(sketch, "E288.trimOffspring", {"start": v(-842.5, -755) * mm, "end": v(-707.5, -755) * mm});
            skLineSegment(sketch, "E289", {"start": v(1242.5, -1350) * mm, "end": v(1257.5, -1350) * mm});
            skLineSegment(sketch, "E290", {"start": v(-699.99, 1260) * mm, "end": v(-1307.5, 1260.55) * mm});
            skLineSegment(sketch, "E291", {"start": v(-1307.5, -1350) * mm, "end": v(-1307.5, 1260.55) * mm});
            skSolve(sketch);
        }
        {
            var Q0;
            Q0 = qSketchRegion(id + "F2", true);
            extrude(context, id + "F3", {"entities" : qUnion([Q0]), "depth" : 150 * mm, "offsetDistance" : 25 * mm});
        }
        {
            var Q0;
            Q0=makeQuery(id+"F3.opExtrude","CAP_EDGE",EDGE,{"disambiguationData":[OSD([sQuery(id+"F2.wireOp",EDGE,"E64.right")])],"isStart":false});
            var Q1;
            Q1=makeQuery(id+"F3.opExtrude","CAP_EDGE",EDGE,{"disambiguationData":[OSD([sQuery(id+"F2.wireOp",EDGE,"E63.right")])],"isStart":false});
            var Q2;
            Q2=makeQuery(id+"F3.opExtrude","CAP_EDGE",EDGE,{"disambiguationData":[OSD([sQuery(id+"F2.wireOp",EDGE,"E62.right")])],"isStart":false});
            var Q3;
            Q3=makeQuery(id+"F3.opExtrude","CAP_EDGE",EDGE,{"disambiguationData":[OSD([sQuery(id+"F2.wireOp",EDGE,"E61.right")])],"isStart":false});
            fillet(context, id + "F4", {"entities" : qUnion([Q0, Q1, Q2, Q3]), "radius" : 120 * mm, "tangentPropagation" : true, "allowEdgeOverflow" : false});
        }
        {
            var Q0;
            Q0=makeQuery(id+"F1.opExtrude","SWEPT_FACE",FACE,{"disambiguationData":[OSD([sQuery(id+"F0.wireOp",EDGE,"E0.right")])]});
            var sketch = newSketch(context, id + "F5", { "sketchPlane" : qUnion([Q0])});
            skLineSegment(sketch, "E292.bottom", {"start": v(-100, 1350) * mm, "end": v(210, 1350) * mm});
            skLineSegment(sketch, "E292.top", {"start": v(-100, -1350) * mm, "end": v(210, -1350) * mm});
            skLineSegment(sketch, "E292.left", {"start": v(-100, 1350) * mm, "end": v(-100, -1350) * mm});
            skLineSegment(sketch, "E292.right", {"start": v(210, 1350) * mm, "end": v(210, -1350) * mm});
            skSolve(sketch);
        }
        {
            var Q0;
            Q0 = qSketchRegion(id + "F5", true);
            extrude(context, id + "F6", {"entities" : qUnion([Q0]), "operationType" : NewBodyOperationType.ADD, "depth" : 100 * mm, "offsetDistance" : 25 * mm});
        }
        {
            var Q0;
            Q0=makeQuery(id+"F1.opExtrude","SWEPT_FACE",FACE,{"disambiguationData":[OSD([sQuery(id+"F0.wireOp",EDGE,"E0.left")])]});
            var sketch = newSketch(context, id + "F7", { "sketchPlane" : qUnion([Q0])});
            skLineSegment(sketch, "E293.bottom", {"start": v(100, 1350) * mm, "end": v(-415, 1350) * mm});
            skLineSegment(sketch, "E293.top", {"start": v(100, -1350) * mm, "end": v(-415, -1350) * mm});
            skLineSegment(sketch, "E293.left", {"start": v(100, 1350) * mm, "end": v(100, -1350) * mm});
            skLineSegment(sketch, "E293.right", {"start": v(-415, 1350) * mm, "end": v(-415, -1350) * mm});
            skSolve(sketch);
        }
        {
            var Q0;
            Q0 = qSketchRegion(id + "F7", true);
            extrude(context, id + "F8", {"entities" : qUnion([Q0]), "operationType" : NewBodyOperationType.ADD, "depth" : 100 * mm, "offsetDistance" : 25 * mm});
        }
        {
            var Q0;
            Q0=makeQuery(id+"F3.opExtrude","CAP_FACE",FACE,{"disambiguationData":[OSD([sQuery(id+"F2.wireOp",EDGE,"E3.top"),sQuery(id+"F2.wireOp",EDGE,"E4.top"),sQuery(id+"F2.wireOp",EDGE,"E5.MirrorCS"),sQuery(id+"F2.wireOp",EDGE,"E6.MirrorCS"),sQuery(id+"F2.wireOp",EDGE,"E7.MirrorCS"),sQuery(id+"F2.wireOp",EDGE,"E8.MirrorCS"),sQuery(id+"F2.wireOp",EDGE,"E9.MirrorCS"),sQuery(id+"F2.wireOp",EDGE,"E10.MirrorCS"),sQuery(id+"F2.wireOp",EDGE,"E11.MirrorCS"),sQuery(id+"F2.wireOp",EDGE,"E13.trimOffspring"),sQuery(id+"F2.wireOp",EDGE,"E12"),sQuery(id+"F2.wireOp",EDGE,"E15.MirrorCS"),sQuery(id+"F2.wireOp",EDGE,"E16.MirrorCS"),sQuery(id+"F2.wireOp",EDGE,"E17.MirrorCS"),sQuery(id+"F2.wireOp",EDGE,"E18.MirrorCS"),sQuery(id+"F2.wireOp",EDGE,"E19.MirrorCS"),sQuery(id+"F2.wireOp",EDGE,"E20.MirrorCS"),sQuery(id+"F2.wireOp",EDGE,"E21"),sQuery(id+"F2.wireOp",EDGE,"E23"),sQuery(id+"F2.wireOp",EDGE,"E24"),sQuery(id+"F2.wireOp",EDGE,"E25.MirrorCS"),sQuery(id+"F2.wireOp",EDGE,"E26.MirrorCS"),sQuery(id+"F2.wireOp",EDGE,"E27.MirrorCS"),sQuery(id+"F2.wireOp",EDGE,"E28.MirrorCS"),sQuery(id+"F2.wireOp",EDGE,"E29.MirrorCS"),sQuery(id+"F2.wireOp",EDGE,"E30.MirrorCS"),sQuery(id+"F2.wireOp",EDGE,"E31.MirrorCS"),sQuery(id+"F2.wireOp",EDGE,"E32.MirrorCS"),sQuery(id+"F2.wireOp",EDGE,"E33"),sQuery(id+"F2.wireOp",EDGE,"E34"),sQuery(id+"F2.wireOp",EDGE,"E35"),sQuery(id+"F2.wireOp",EDGE,"E36"),sQuery(id+"F2.wireOp",EDGE,"E37"),sQuery(id+"F2.wireOp",EDGE,"E42.MirrorCS"),sQuery(id+"F2.wireOp",EDGE,"E43.MirrorCS"),sQuery(id+"F2.wireOp",EDGE,"E44.MirrorCS"),sQuery(id+"F2.wireOp",EDGE,"E45.MirrorCS"),sQuery(id+"F2.wireOp",EDGE,"E46.MirrorCS"),sQuery(id+"F2.wireOp",EDGE,"E47.MirrorCS"),sQuery(id+"F2.wireOp",EDGE,"E48.MirrorCS"),sQuery(id+"F2.wireOp",EDGE,"E49.MirrorCS"),sQuery(id+"F2.wireOp",EDGE,"E50.MirrorCS"),sQuery(id+"F2.wireOp",EDGE,"E56"),sQuery(id+"F2.wireOp",EDGE,"E57"),sQuery(id+"F2.wireOp",EDGE,"E58"),sQuery(id+"F2.wireOp",EDGE,"E59"),sQuery(id+"F2.wireOp",EDGE,"E22"),sQuery(id+"F2.wireOp",EDGE,"E61.right"),sQuery(id+"F2.wireOp",EDGE,"E62.right"),sQuery(id+"F2.wireOp",EDGE,"E63.right"),sQuery(id+"F2.wireOp",EDGE,"E64.right"),sQuery(id+"F2.wireOp",EDGE,"E66.trimOffspring"),sQuery(id+"F2.wireOp",EDGE,"E67.trimOffspring"),sQuery(id+"F2.wireOp",EDGE,"E68.trimOffspring"),sQuery(id+"F2.wireOp",EDGE,"E69.trimOffspring"),sQuery(id+"F2.wireOp",EDGE,"E70.trimOffspring"),sQuery(id+"F2.wireOp",EDGE,"E71.trimOffspring"),sQuery(id+"F2.wireOp",EDGE,"E72.trimOffspring"),sQuery(id+"F2.wireOp",EDGE,"E73.trimOffspring"),sQuery(id+"F2.wireOp",EDGE,"E74.trimOffspring"),sQuery(id+"F2.wireOp",EDGE,"E75.trimOffspring"),sQuery(id+"F2.wireOp",EDGE,"E76.trimOffspring"),sQuery(id+"F2.wireOp",EDGE,"E77.trimOffspring"),sQuery(id+"F2.wireOp",EDGE,"E78.trimOffspring"),sQuery(id+"F2.wireOp",EDGE,"E79.trimOffspring"),sQuery(id+"F2.wireOp",EDGE,"E80.trimOffspring"),sQuery(id+"F2.wireOp",EDGE,"E81.trimOffspring"),sQuery(id+"F2.wireOp",EDGE,"E82.trimOffspring"),sQuery(id+"F2.wireOp",EDGE,"E83.trimOffspring"),sQuery(id+"F2.wireOp",EDGE,"E84.trimOffspring"),sQuery(id+"F2.wireOp",EDGE,"E85.trimOffspring"),sQuery(id+"F2.wireOp",EDGE,"E86.trimOffspring"),sQuery(id+"F2.wireOp",EDGE,"E87.trimOffspring"),sQuery(id+"F2.wireOp",EDGE,"E88.trimOffspring"),sQuery(id+"F2.wireOp",EDGE,"E89"),sQuery(id+"F2.wireOp",EDGE,"E90.trimOffspring"),sQuery(id+"F2.wireOp",EDGE,"E91.trimOffspring"),sQuery(id+"F2.wireOp",EDGE,"E92.trimOffspring"),sQuery(id+"F2.wireOp",EDGE,"E93.trimOffspring"),sQuery(id+"F2.wireOp",EDGE,"E94.trimOffspring"),sQuery(id+"F2.wireOp",EDGE,"E95.trimOffspring"),sQuery(id+"F2.wireOp",EDGE,"E96.trimOffspring"),sQuery(id+"F2.wireOp",EDGE,"E97.trimOffspring"),sQuery(id+"F2.wireOp",EDGE,"E98"),sQuery(id+"F2.wireOp",EDGE,"E99.trimOffspring"),sQuery(id+"F2.wireOp",EDGE,"E100.trimOffspring"),sQuery(id+"F2.wireOp",EDGE,"E101.trimOffspring"),sQuery(id+"F2.wireOp",EDGE,"E102.trimOffspring"),sQuery(id+"F2.wireOp",EDGE,"E103.trimOffspring"),sQuery(id+"F2.wireOp",EDGE,"E104.trimOffspring"),sQuery(id+"F2.wireOp",EDGE,"E105.trimOffspring"),sQuery(id+"F2.wireOp",EDGE,"E106.trimOffspring"),sQuery(id+"F2.wireOp",EDGE,"E107.trimOffspring"),sQuery(id+"F2.wireOp",EDGE,"E108.trimOffspring"),sQuery(id+"F2.wireOp",EDGE,"E109.trimOffspring"),sQuery(id+"F2.wireOp",EDGE,"E110.trimOffspring"),sQuery(id+"F2.wireOp",EDGE,"E111.trimOffspring"),sQuery(id+"F2.wireOp",EDGE,"E112.trimOffspring"),sQuery(id+"F2.wireOp",EDGE,"E113.trimOffspring"),sQuery(id+"F2.wireOp",EDGE,"E114.trimOffspring"),sQuery(id+"F2.wireOp",EDGE,"E115.trimOffspring"),sQuery(id+"F2.wireOp",EDGE,"E116.trimOffspring"),sQuery(id+"F2.wireOp",EDGE,"E117.trimOffspring"),sQuery(id+"F2.wireOp",EDGE,"E118.trimOffspring"),sQuery(id+"F2.wireOp",EDGE,"E119.trimOffspring"),sQuery(id+"F2.wireOp",EDGE,"E120.trimOffspring"),sQuery(id+"F2.wireOp",EDGE,"E121.trimOffspring"),sQuery(id+"F2.wireOp",EDGE,"E122.trimOffspring"),sQuery(id+"F2.wireOp",EDGE,"E123.trimOffspring"),sQuery(id+"F2.wireOp",EDGE,"E124.trimOffspring"),sQuery(id+"F2.wireOp",EDGE,"E125.trimOffspring"),sQuery(id+"F2.wireOp",EDGE,"E126.trimOffspring"),sQuery(id+"F2.wireOp",EDGE,"E127.trimOffspring"),sQuery(id+"F2.wireOp",EDGE,"E128.trimOffspring"),sQuery(id+"F2.wireOp",EDGE,"E129.trimOffspring"),sQuery(id+"F2.wireOp",EDGE,"E130.trimOffspring"),sQuery(id+"F2.wireOp",EDGE,"E131.trimOffspring"),sQuery(id+"F2.wireOp",EDGE,"E132.trimOffspring"),sQuery(id+"F2.wireOp",EDGE,"E133.trimOffspring"),sQuery(id+"F2.wireOp",EDGE,"E134.trimOffspring"),sQuery(id+"F2.wireOp",EDGE,"E135.trimOffspring"),sQuery(id+"F2.wireOp",EDGE,"E136.trimOffspring"),sQuery(id+"F2.wireOp",EDGE,"E137.trimOffspring"),sQuery(id+"F2.wireOp",EDGE,"E138.trimOffspring"),sQuery(id+"F2.wireOp",EDGE,"E139.trimOffspring"),sQuery(id+"F2.wireOp",EDGE,"E140.trimOffspring"),sQuery(id+"F2.wireOp",EDGE,"E141.trimOffspring"),sQuery(id+"F2.wireOp",EDGE,"E142.trimOffspring"),sQuery(id+"F2.wireOp",EDGE,"E143.trimOffspring"),sQuery(id+"F2.wireOp",EDGE,"E144.trimOffspring"),sQuery(id+"F2.wireOp",EDGE,"E145.trimOffspring"),sQuery(id+"F2.wireOp",EDGE,"E146.trimOffspring"),sQuery(id+"F2.wireOp",EDGE,"E147.trimOffspring"),sQuery(id+"F2.wireOp",EDGE,"E148.trimOffspring"),sQuery(id+"F2.wireOp",EDGE,"E149.trimOffspring"),sQuery(id+"F2.wireOp",EDGE,"E150.trimOffspring"),sQuery(id+"F2.wireOp",EDGE,"E151.trimOffspring"),sQuery(id+"F2.wireOp",EDGE,"E152.trimOffspring"),sQuery(id+"F2.wireOp",EDGE,"E153.trimOffspring"),sQuery(id+"F2.wireOp",EDGE,"E154.trimOffspring"),sQuery(id+"F2.wireOp",EDGE,"E155.trimOffspring"),sQuery(id+"F2.wireOp",EDGE,"E156.trimOffspring"),sQuery(id+"F2.wireOp",EDGE,"E157.trimOffspring"),sQuery(id+"F2.wireOp",EDGE,"E158.trimOffspring"),sQuery(id+"F2.wireOp",EDGE,"E159.trimOffspring"),sQuery(id+"F2.wireOp",EDGE,"E160.trimOffspring"),sQuery(id+"F2.wireOp",EDGE,"E161.trimOffspring"),sQuery(id+"F2.wireOp",EDGE,"E162.trimOffspring"),sQuery(id+"F2.wireOp",EDGE,"E163.trimOffspring"),sQuery(id+"F2.wireOp",EDGE,"E164.trimOffspring"),sQuery(id+"F2.wireOp",EDGE,"E165.trimOffspring"),sQuery(id+"F2.wireOp",EDGE,"E166.trimOffspring"),sQuery(id+"F2.wireOp",EDGE,"E167.trimOffspring"),sQuery(id+"F2.wireOp",EDGE,"E168.trimOffspring"),sQuery(id+"F2.wireOp",EDGE,"E169.trimOffspring"),sQuery(id+"F2.wireOp",EDGE,"E170.trimOffspring"),sQuery(id+"F2.wireOp",EDGE,"E171.trimOffspring"),sQuery(id+"F2.wireOp",EDGE,"E172.trimOffspring"),sQuery(id+"F2.wireOp",EDGE,"E173.trimOffspring"),sQuery(id+"F2.wireOp",EDGE,"E174.trimOffspring"),sQuery(id+"F2.wireOp",EDGE,"E175.trimOffspring"),sQuery(id+"F2.wireOp",EDGE,"E176.trimOffspring"),sQuery(id+"F2.wireOp",EDGE,"E177.trimOffspring"),sQuery(id+"F2.wireOp",EDGE,"E178.trimOffspring"),sQuery(id+"F2.wireOp",EDGE,"E179.trimOffspring"),sQuery(id+"F2.wireOp",EDGE,"E180.trimOffspring"),sQuery(id+"F2.wireOp",EDGE,"E181.trimOffspring"),sQuery(id+"F2.wireOp",EDGE,"E182"),sQuery(id+"F2.wireOp",EDGE,"E183.trimOffspring"),sQuery(id+"F2.wireOp",EDGE,"E184.trimOffspring"),sQuery(id+"F2.wireOp",EDGE,"E185.trimOffspring"),sQuery(id+"F2.wireOp",EDGE,"E186.trimOffspring"),sQuery(id+"F2.wireOp",EDGE,"E187.trimOffspring"),sQuery(id+"F2.wireOp",EDGE,"E188.trimOffspring"),sQuery(id+"F2.wireOp",EDGE,"E189.trimOffspring"),sQuery(id+"F2.wireOp",EDGE,"E190.trimOffspring"),sQuery(id+"F2.wireOp",EDGE,"E191.trimOffspring"),sQuery(id+"F2.wireOp",EDGE,"E192.trimOffspring"),sQuery(id+"F2.wireOp",EDGE,"E193.trimOffspring"),sQuery(id+"F2.wireOp",EDGE,"E194.trimOffspring"),sQuery(id+"F2.wireOp",EDGE,"E195.trimOffspring"),sQuery(id+"F2.wireOp",EDGE,"E196.trimOffspring"),sQuery(id+"F2.wireOp",EDGE,"E197.trimOffspring"),sQuery(id+"F2.wireOp",EDGE,"E198.trimOffspring"),sQuery(id+"F2.wireOp",EDGE,"E199.trimOffspring"),sQuery(id+"F2.wireOp",EDGE,"E200.trimOffspring"),sQuery(id+"F2.wireOp",EDGE,"E201.trimOffspring"),sQuery(id+"F2.wireOp",EDGE,"E202.trimOffspring"),sQuery(id+"F2.wireOp",EDGE,"E203.trimOffspring"),sQuery(id+"F2.wireOp",EDGE,"E204.trimOffspring"),sQuery(id+"F2.wireOp",EDGE,"E205.trimOffspring"),sQuery(id+"F2.wireOp",EDGE,"E206.trimOffspring"),sQuery(id+"F2.wireOp",EDGE,"E207.trimOffspring"),sQuery(id+"F2.wireOp",EDGE,"E208.trimOffspring"),sQuery(id+"F2.wireOp",EDGE,"E209.trimOffspring"),sQuery(id+"F2.wireOp",EDGE,"E210.trimOffspring"),sQuery(id+"F2.wireOp",EDGE,"E211.trimOffspring"),sQuery(id+"F2.wireOp",EDGE,"E212.trimOffspring"),sQuery(id+"F2.wireOp",EDGE,"E213.trimOffspring"),sQuery(id+"F2.wireOp",EDGE,"E214.trimOffspring"),sQuery(id+"F2.wireOp",EDGE,"E215.trimOffspring"),sQuery(id+"F2.wireOp",EDGE,"E216.trimOffspring"),sQuery(id+"F2.wireOp",EDGE,"E217.trimOffspring"),sQuery(id+"F2.wireOp",EDGE,"E218.trimOffspring"),sQuery(id+"F2.wireOp",EDGE,"E219.trimOffspring"),sQuery(id+"F2.wireOp",EDGE,"E220.trimOffspring"),sQuery(id+"F2.wireOp",EDGE,"E221.trimOffspring"),sQuery(id+"F2.wireOp",EDGE,"E222.trimOffspring"),sQuery(id+"F2.wireOp",EDGE,"E223.trimOffspring"),sQuery(id+"F2.wireOp",EDGE,"E224.trimOffspring"),sQuery(id+"F2.wireOp",EDGE,"E225.trimOffspring"),sQuery(id+"F2.wireOp",EDGE,"E226.trimOffspring"),sQuery(id+"F2.wireOp",EDGE,"E227.trimOffspring"),sQuery(id+"F2.wireOp",EDGE,"E228.trimOffspring"),sQuery(id+"F2.wireOp",EDGE,"E229.trimOffspring"),sQuery(id+"F2.wireOp",EDGE,"E230.trimOffspring"),sQuery(id+"F2.wireOp",EDGE,"E231.trimOffspring"),sQuery(id+"F2.wireOp",EDGE,"E232.trimOffspring"),sQuery(id+"F2.wireOp",EDGE,"E233.trimOffspring"),sQuery(id+"F2.wireOp",EDGE,"E234.trimOffspring"),sQuery(id+"F2.wireOp",EDGE,"E235.trimOffspring"),sQuery(id+"F2.wireOp",EDGE,"E236.trimOffspring"),sQuery(id+"F2.wireOp",EDGE,"E237.trimOffspring"),sQuery(id+"F2.wireOp",EDGE,"E238.trimOffspring"),sQuery(id+"F2.wireOp",EDGE,"E239.trimOffspring"),sQuery(id+"F2.wireOp",EDGE,"E240.trimOffspring"),sQuery(id+"F2.wireOp",EDGE,"E241.trimOffspring"),sQuery(id+"F2.wireOp",EDGE,"E242.trimOffspring"),sQuery(id+"F2.wireOp",EDGE,"E243.trimOffspring"),sQuery(id+"F2.wireOp",EDGE,"E244.trimOffspring"),sQuery(id+"F2.wireOp",EDGE,"E245.trimOffspring"),sQuery(id+"F2.wireOp",EDGE,"E246.trimOffspring"),sQuery(id+"F2.wireOp",EDGE,"E247.trimOffspring"),sQuery(id+"F2.wireOp",EDGE,"E248.trimOffspring"),sQuery(id+"F2.wireOp",EDGE,"E249.trimOffspring"),sQuery(id+"F2.wireOp",EDGE,"E250.trimOffspring"),sQuery(id+"F2.wireOp",EDGE,"E251.trimOffspring"),sQuery(id+"F2.wireOp",EDGE,"E252.trimOffspring"),sQuery(id+"F2.wireOp",EDGE,"E253.trimOffspring"),sQuery(id+"F2.wireOp",EDGE,"E254.trimOffspring"),sQuery(id+"F2.wireOp",EDGE,"E255.trimOffspring"),sQuery(id+"F2.wireOp",EDGE,"E256.trimOffspring"),sQuery(id+"F2.wireOp",EDGE,"E257.trimOffspring"),sQuery(id+"F2.wireOp",EDGE,"E258.trimOffspring"),sQuery(id+"F2.wireOp",EDGE,"E259.trimOffspring"),sQuery(id+"F2.wireOp",EDGE,"E260.trimOffspring"),sQuery(id+"F2.wireOp",EDGE,"E261.trimOffspring"),sQuery(id+"F2.wireOp",EDGE,"E262.trimOffspring"),sQuery(id+"F2.wireOp",EDGE,"E263.trimOffspring"),sQuery(id+"F2.wireOp",EDGE,"E264.trimOffspring"),sQuery(id+"F2.wireOp",EDGE,"E265.trimOffspring"),sQuery(id+"F2.wireOp",EDGE,"E266.trimOffspring"),sQuery(id+"F2.wireOp",EDGE,"E267.trimOffspring"),sQuery(id+"F2.wireOp",EDGE,"E268.trimOffspring"),sQuery(id+"F2.wireOp",EDGE,"E269.trimOffspring"),sQuery(id+"F2.wireOp",EDGE,"E270.trimOffspring"),sQuery(id+"F2.wireOp",EDGE,"E271.trimOffspring"),sQuery(id+"F2.wireOp",EDGE,"E272.trimOffspring"),sQuery(id+"F2.wireOp",EDGE,"E273.trimOffspring"),sQuery(id+"F2.wireOp",EDGE,"E274.trimOffspring"),sQuery(id+"F2.wireOp",EDGE,"E275.trimOffspring"),sQuery(id+"F2.wireOp",EDGE,"E276.trimOffspring"),sQuery(id+"F2.wireOp",EDGE,"E277.trimOffspring"),sQuery(id+"F2.wireOp",EDGE,"E278.trimOffspring"),sQuery(id+"F2.wireOp",EDGE,"E279.trimOffspring"),sQuery(id+"F2.wireOp",EDGE,"E280.trimOffspring"),sQuery(id+"F2.wireOp",EDGE,"E281.trimOffspring"),sQuery(id+"F2.wireOp",EDGE,"E282.trimOffspring"),sQuery(id+"F2.wireOp",EDGE,"E283.trimOffspring"),sQuery(id+"F2.wireOp",EDGE,"E284.trimOffspring"),sQuery(id+"F2.wireOp",EDGE,"E285.trimOffspring"),sQuery(id+"F2.wireOp",EDGE,"E286.trimOffspring"),sQuery(id+"F2.wireOp",EDGE,"E287.trimOffspring"),sQuery(id+"F2.wireOp",EDGE,"E288.trimOffspring"),sQuery(id+"F2.wireOp",EDGE,"E289"),sQuery(id+"F2.wireOp",EDGE,"E290"),sQuery(id+"F2.wireOp",EDGE,"E291")])],"isStart":false});
            var sketch = newSketch(context, id + "F9", { "sketchPlane" : qUnion([Q0])});
            skLineSegment(sketch, "E294.bottom", {"start": v(-1292.5, -1155) * mm, "end": v(1242.5, -1155) * mm});
            skLineSegment(sketch, "E294.top", {"start": v(-1292.5, -1350) * mm, "end": v(1242.5, -1350) * mm});
            skLineSegment(sketch, "E294.left", {"start": v(-1292.5, -1155) * mm, "end": v(-1292.5, -1350) * mm});
            skLineSegment(sketch, "E294.right", {"start": v(1242.5, -1155) * mm, "end": v(1242.5, -1350) * mm});
            skSolve(sketch);
        }
        {
            var Q0;
            Q0 = qSketchRegion(id + "F9", true);
            extrude(context, id + "F10", {"entities" : qUnion([Q0]), "operationType" : NewBodyOperationType.ADD, "oppositeDirection" : true, "depth" : 15 * mm, "offsetDistance" : 25 * mm});
        }
        {
            var Q0;
            Q0=makeQuery(id+"F8.boolean.opBoolean","MERGE",FACE,{"derivedFrom":[makeQuery(id+"F6.boolean.opBoolean","MERGE",FACE,{"derivedFrom":[makeQuery(id+"F1.opExtrude","SWEPT_FACE",FACE,{"disambiguationData":[OSD([sQuery(id+"F0.wireOp",EDGE,"E0.bottom")])]}),makeQuery(id+"F6.opExtrude","SWEPT_FACE",FACE,{"disambiguationData":[OSD([sQuery(id+"F5.wireOp",EDGE,"E292.top")])]})]}),makeQuery(id+"F8.opExtrude","SWEPT_FACE",FACE,{"disambiguationData":[OSD([sQuery(id+"F7.wireOp",EDGE,"E293.top")])]})]});
            var sketch = newSketch(context, id + "F11", { "sketchPlane" : qUnion([Q0])});
            skLineSegment(sketch, "E295.bottom", {"start": v(-1450, -100) * mm, "end": v(1450, -100) * mm});
            skLineSegment(sketch, "E295.top", {"start": v(-1450, 415) * mm, "end": v(1450, 415) * mm});
            skLineSegment(sketch, "E295.left", {"start": v(-1450, -100) * mm, "end": v(-1450, 415) * mm});
            skLineSegment(sketch, "E295.right", {"start": v(1450, -100) * mm, "end": v(1450, 415) * mm});
            skSolve(sketch);
        }
        {
            var Q0;
            Q0 = qSketchRegion(id + "F11", true);
            extrude(context, id + "F12", {"entities" : qUnion([Q0]), "depth" : 100 * mm, "offsetDistance" : 25 * mm});
        }
    });
